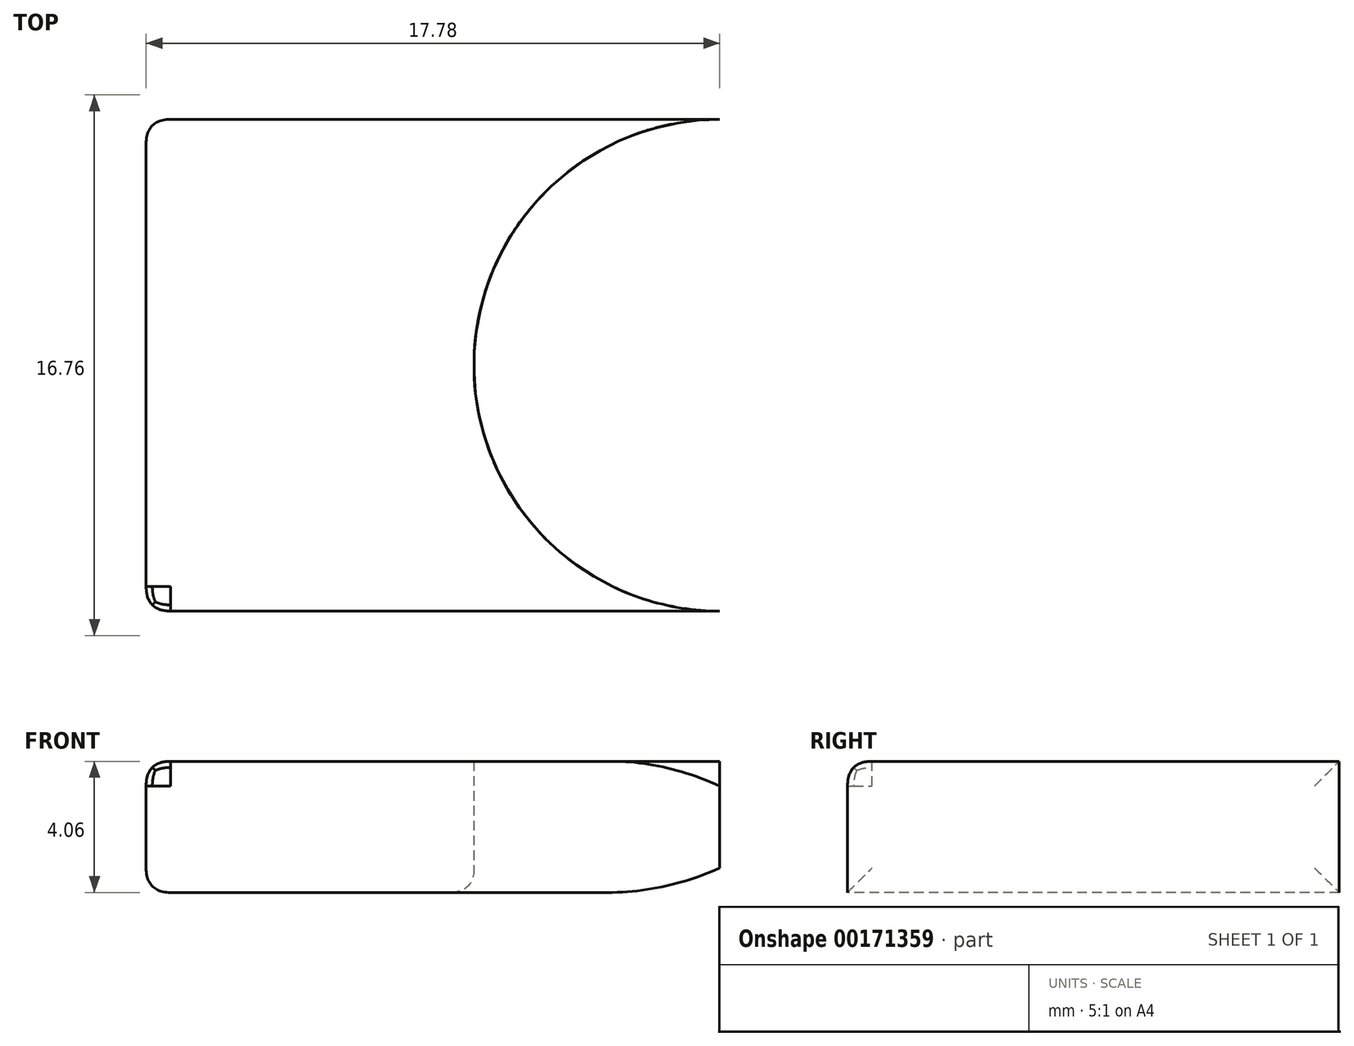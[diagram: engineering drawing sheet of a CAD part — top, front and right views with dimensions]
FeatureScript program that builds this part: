
annotation { "Feature Type Name" : "Feature", "Feature Type Description" : "" }
export const myFeature = defineFeature(function(context is Context, id is Id, definition is map)
    precondition{}
    {
        {
            var Q0;
            Q0=qCreatedBy(makeId("Top.planeOp"),FACE);
            var sketch = newSketch(context, id + "F0", { "sketchPlane" : qUnion([Q0])});
            skCircle(sketch, "E0", {"center": v(0, 0) * mm, "radius": 7.62 * mm});
            skLineSegment(sketch, "E1.bottom", {"start": v(0, 7.62) * mm, "end": v(-17.78, 7.62) * mm});
            skLineSegment(sketch, "E1.top", {"start": v(0, -7.62) * mm, "end": v(-17.78, -7.62) * mm});
            skLineSegment(sketch, "E1.left", {"start": v(0, 7.62) * mm, "end": v(0, -7.62) * mm});
            skLineSegment(sketch, "E1.right", {"start": v(-17.78, 7.62) * mm, "end": v(-17.78, -7.62) * mm});
            skLineSegment(sketch, "E2.bottom", {"start": v(0, -7.62) * mm, "end": v(0, -7.62) * mm});
            skLineSegment(sketch, "E2.top", {"start": v(0, 7.62) * mm, "end": v(0, 7.62) * mm});
            skLineSegment(sketch, "E2.right", {"start": v(0, -7.62) * mm, "end": v(0, 7.62) * mm});
            skSolve(sketch);
        }
        {
            var Q0;
            {var subQ1=sQuery(id+"F0.wireOp",EDGE,"E1.bottom");Q0=makeQuery(id+"F0.imprint","IMPRINT",FACE,{"disambiguationData":[TD([[makeQuery(id+"F0.imprint","IMPRINT",EDGE,{"derivedFrom":subQ1}),1.0]])]});}
            var Q1;
            {var subQ0=sQuery(id+"F0.wireOp",EDGE,"E2.right");Q1=makeQuery(id+"F0.imprint","IMPRINT",FACE,{"disambiguationData":[TD([[makeQuery(id+"F0.imprint","IMPRINT",EDGE,{"derivedFrom":subQ0}),1.0]])]});}
            var Q2;
            {var subQ0=sQuery(id+"F0.wireOp",EDGE,"E2.right");Q2=makeQuery(id+"F0.imprint","IMPRINT",FACE,{"disambiguationData":[TD([[makeQuery(id+"F0.imprint","IMPRINT",EDGE,{"derivedFrom":subQ0}),-1.0]])]});}
            extrude(context, id + "F1", {"entities" : qUnion([Q0, Q1, Q2]), "depth" : 4.06 * mm});
        }
        {
            var Q0;
            Q0=makeQuery(id+"F1.opExtrude","CAP_FACE",FACE,{"disambiguationData":[OSD([sQuery(id+"F0.wireOp",EDGE,"E0"),sQuery(id+"F0.wireOp",EDGE,"E1.bottom"),sQuery(id+"F0.wireOp",EDGE,"E1.top"),sQuery(id+"F0.wireOp",EDGE,"E1.right")])],"isStart":false});
            var sketch = newSketch(context, id + "F2", { "sketchPlane" : qUnion([Q0])});
            skPoint(sketch, "E3", {"position": v(0, 0) * mm});
            skSolve(sketch);
        }
        {
            var Q0;
            Q0=sQuery(id+"F2.wireOp",VERTEX,"E3");
            var Q1;
            Q1=makeQuery(id+"F1.opExtrude","SWEPT_BODY",BODY,{"disambiguationData":[OSD([sQuery(id+"F0.wireOp",EDGE,"E0"),sQuery(id+"F0.wireOp",EDGE,"E1.bottom"),sQuery(id+"F0.wireOp",EDGE,"E1.top"),sQuery(id+"F0.wireOp",EDGE,"E1.right")])]});
            hole(context, id + "F3", {"style" : HoleStyle.SIMPLE, "endStyle" : HoleEndStyle.THROUGH, "holeDiameter" : 6.86 * mm, "locations" : qUnion([Q0]), "scope" : qUnion([Q1]), "isTappedThrough" : true});
        }
        {
            var Q0;
            Q0=makeQuery(id+"F1.opExtrude","CAP_EDGE",EDGE,{"disambiguationData":[OSD([sQuery(id+"F0.wireOp",EDGE,"E1.top")])],"isStart":false});
            var Q1;
            Q1=makeQuery(id+"F1.opExtrude","CAP_EDGE",EDGE,{"disambiguationData":[OSD([sQuery(id+"F0.wireOp",EDGE,"E0")])],"isStart":true});
            var Q2;
            Q2=makeQuery(id+"F1.opExtrude","SWEPT_FACE",FACE,{"disambiguationData":[OSD([sQuery(id+"F0.wireOp",EDGE,"E1.right")])]});
            fillet(context, id + "F4", {"entities" : qUnion([Q0, Q1, Q2]), "radius" : 0.76 * mm, "tangentPropagation" : true, "rho" : 0.5, "crossSection" : FilletCrossSection.CONIC, "allowEdgeOverflow" : false});
        }
    });
